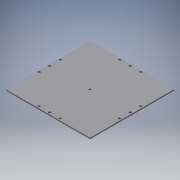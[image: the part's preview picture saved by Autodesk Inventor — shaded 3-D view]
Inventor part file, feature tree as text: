
AUTODESK INVENTOR PART (.ipt)
format: ipt  version: 2019 (Build 230136000, 136)  size: 132,608 bytes
history: native  units: mm
features: extrude x2, sketch x2, plane x1, pattern_circular x1, reference x1, projected_geometry x1
ambient origin geometry x8: Origin, YZ Plane, XZ Plane, XY Plane, X Axis, Y Axis, Z Axis, Center Point
bodies: Volumenkörper1 (feature_tree)
feature tree (8):
  plane  "Arbeitsebene1"
  extrude  "Extrusion1"  Depth=65.0mm
  extrude  "Extrusion2"  Depth=1.0mm
  pattern_circular  "Runde Anordnung1"  [2 undecoded]
  sketch  "Skizze1"  dims[d0=65.0mm d1=65.0mm]
  reference  "Referenz1"
  sketch  "Skizze2"  dims[d2=1.0mm d3=0.0mm d4=2.0mm d5=2.0mm d6=1.4mm d7=1.4mm d8=2.0mm d9=2.0mm d10=2.0mm d11=2.0mm d12=1.0mm d13=0.0mm d14=40.0mm d15=360.0deg]
  projected_geometry  "Projizierte Kontur1"
note: 2 required parameter values undecoded (feature->parameter linkage not recoverable at this tier; creation-order binding heuristic only, values carry confidence <= 0.55)
